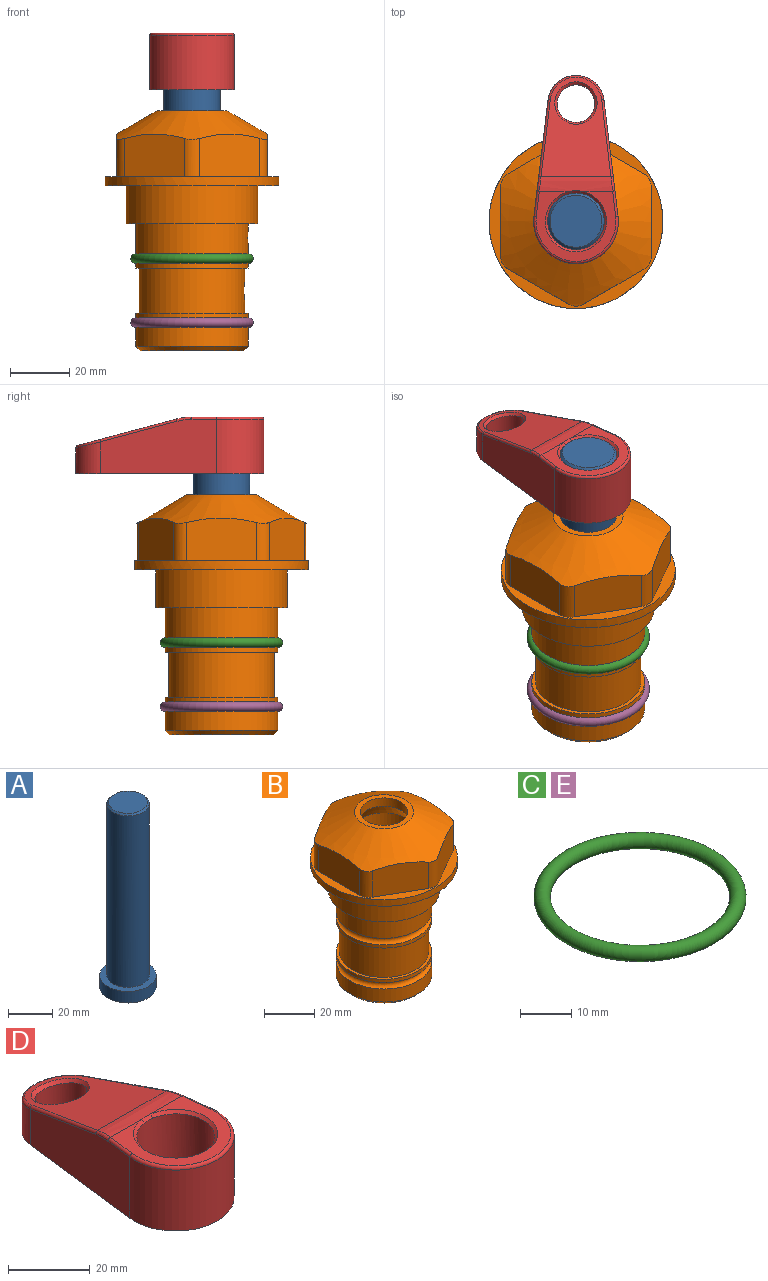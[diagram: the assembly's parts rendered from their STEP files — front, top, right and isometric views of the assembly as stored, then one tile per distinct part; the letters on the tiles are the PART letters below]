
ASSEMBLY  parts=5 mates=4
PART A: 6 faces, bbox 25.4x25.4x101.6 mm
  f0: plane 17.46x17.46mm, normal (0,0,1), area 239.5mm2, adj f5
  f1: plane 25.4x25.4mm, normal (0,0,-1), area 506.7mm2, adj f2
  f2: cylinder r=12.7mm len=25.4mm, axis (0,0,1), area 506.7mm2, adj f1,f3
  f3: plane 25.4x25.4mm, normal (0,0,1), area 221.7mm2, adj f2,f4
  f4: cylinder r=9.53mm len=94.46mm, axis (0,0,1), area 5653mm2, adj f3,f5
  f5: cone r=8.73mm half-angle=45deg, axis (0,0,-1), area 64.4mm2, adj f0,f4
PART B: 36 faces, bbox 58.7x58.7x81 mm
  f0: cylinder r=17.78mm len=35.56mm, axis (0,0,1), area 1670.8mm2, adj f23,f24,f31
  f1: cylinder r=19.05mm len=38.1mm, axis (0,0,1), area 1191.9mm2, adj f26,f27,f30
  f2: plane 58.66x58.66mm, normal (0,0,-1), area 1150.6mm2, adj f3,f28
  f3: cylinder r=29.33mm len=58.66mm, axis (0,0,-1), area 585.1mm2, adj f2,f4
  f4: plane 58.66x58.66mm, normal (0,0,1), area 475.9mm2, adj f3,f5,f6,f7,f8,f9,f10,f11
  f5: plane 20.32x14.34mm, normal (-0.5,0.87,0), area 324.4mm2, adj f4,f15,f16,f17
  f6: plane 20.32x14.34mm, normal (0.5,0.87,0), area 324.4mm2, adj f4,f14,f15,f17
  f7: plane 23.48x14.34mm, normal (1,0,0), area 324.4mm2, adj f4,f13,f14,f17
  f8: plane 20.32x14.34mm, normal (0.5,-0.87,0), area 324.4mm2, adj f4,f12,f13,f17
  f9: plane 20.32x14.34mm, normal (-0.5,-0.87,0), area 324.4mm2, adj f4,f11,f12,f17
  f10: plane 23.48x14.34mm, normal (-1,0,0), area 324.4mm2, adj f4,f11,f16,f17
  f11: cylinder r=5.08mm len=12.85mm, axis (0,0,-1), area 67.2mm2, adj f4,f9,f10,f17
  f12: cylinder r=5.08mm len=12.85mm, axis (0,0,-1), area 67.2mm2, adj f4,f8,f9,f17
  f13: cylinder r=5.08mm len=12.85mm, axis (0,0,-1), area 67.2mm2, adj f4,f7,f8,f17
  f14: cylinder r=5.08mm len=12.85mm, axis (0,0,-1), area 67.2mm2, adj f4,f6,f7,f17
  f15: cylinder r=5.08mm len=12.85mm, axis (0,0,-1), area 67.2mm2, adj f4,f5,f6,f17
  f16: cylinder r=5.08mm len=12.85mm, axis (0,0,-1), area 67.2mm2, adj f4,f5,f10,f17
  f17: cone r=11.73mm half-angle=60deg, axis (0,0,-1), area 2071.8mm2, adj f5,f6,f7,f8,f9,f10,f11,f12
  f18: plane 23.46x23.46mm, normal (0,0,1), area 147.4mm2, adj f17,f35
  f19: plane 34.93x34.93mm, normal (0,0,-1), area 958mm2, adj f29
  f20: cylinder r=19.05mm len=38.1mm, axis (0,0,1), area 760.1mm2, adj f21,f29
  f21: torus R=19.05mm, axis (0,0,1), area 565.3mm2, adj f20,f22
  f22: cylinder r=19.05mm len=38.1mm, axis (0,0,1), area 190mm2, adj f21,f23
  f23: plane 38.1x38.1mm, normal (0,0,1), area 146.9mm2, adj f0,f22
  f24: plane 38.1x38.1mm, normal (0,0,-1), area 146.9mm2, adj f0,f25
  f25: cylinder r=19.05mm len=38.1mm, axis (0,0,1), area 190mm2, adj f24,f26
  f26: torus R=19.05mm, axis (0,0,1), area 565.3mm2, adj f1,f25
  f27: plane 44.45x44.45mm, normal (0,0,-1), area 411.7mm2, adj f1,f28
  f28: cylinder r=22.23mm len=44.45mm, axis (0,0,1), area 1773.5mm2, adj f2,f27
  f29: cone r=19.05mm half-angle=45deg, axis (0,0,1), area 257.5mm2, adj f19,f20
  f30: cylinder r=3.17mm len=6.75mm, axis (-1,0,0), area 128mm2, adj f1,f33
  f31: cylinder r=3.17mm len=6.35mm, axis (-1,0,0), area 102.5mm2, adj f0,f33
  f32: plane 25.4x25.4mm, normal (0,0,1), area 506.7mm2, adj f33
  f33: cylinder r=12.7mm len=66.42mm, axis (0,0,-1), area 5236.2mm2, adj f30,f31,f32,f34
  f34: cone r=9.53mm half-angle=30deg, axis (0,0,-1), area 443.4mm2, adj f33,f35
  f35: cylinder r=9.53mm len=19.05mm, axis (0,0,-1), area 240.9mm2, adj f18,f34
PART C: 1 faces, bbox 44.7x44.7x3.2 mm
  f0: torus R=19.05mm, axis (0,0,1), area 1193.9mm2
PART D: 31 faces, bbox 31.7x65.5x19.8 mm
  f0: plane 39.12x18.26mm, normal (0.99,0.12,0), area 612.2mm2, adj f1,f4,f7,f11,f13,f15
  f1: cylinder r=9.53mm len=18.91mm, axis (0,0,-1), area 296.1mm2, adj f0,f2,f7,f17
  f2: plane 39.12x18.26mm, normal (-0.99,0.12,0), area 612.2mm2, adj f1,f4,f7,f12,f14,f16
  f3: cylinder r=6.35mm len=12.7mm, axis (0,0,-1), area 362.4mm2, adj f7,f18
  f4: cylinder r=14.29mm len=28.58mm, axis (0,0,-1), area 882.2mm2, adj f0,f2,f7,f10
  f5: cylinder r=9.53mm len=19.05mm, axis (0,0,-1), area 1092.6mm2, adj f7,f19,f20
  f6: plane 26.99x23.69mm, normal (0,0,1), area 216.2mm2, adj f9,f10,f11,f12,f19
  f7: plane 63.5x28.58mm, normal (0,0,-1), area 661.8mm2, adj f0,f1,f2,f3,f4,f5,f22,f23
  f8: plane 33.52x23.6mm, normal (0,0.26,0.97), area 486mm2, adj f9,f15,f16,f17,f18
  f9: cylinder r=19.05mm len=24.72mm, axis (1,0,0), area 120.4mm2, adj f6,f8,f13,f14,f20
  f10: torus R=13.49mm, axis (0,0,1), area 59mm2, adj f4,f6,f11,f12
  f11: cylinder r=0.79mm len=8.67mm, axis (0.12,-0.99,0), area 10.8mm2, adj f0,f6,f10,f13
  f12: cylinder r=0.79mm len=8.67mm, axis (0.12,0.99,0), area 10.8mm2, adj f2,f6,f10,f14
  f13: bspline ~4.95x1.42mm, area 6.1mm2, adj f0,f9,f11,f15
  f14: bspline ~4.95x1.42mm, area 6.1mm2, adj f2,f9,f12,f16
  f15: cylinder r=0.79mm len=25.95mm, axis (0.12,-0.96,0.26), area 32.9mm2, adj f0,f8,f13,f17
  f16: cylinder r=0.79mm len=25.95mm, axis (0.12,0.96,-0.26), area 32.9mm2, adj f2,f8,f14,f17
  f17: bspline ~18.91x8.38mm, area 30mm2, adj f1,f8,f15,f16
  f18: bspline ~14.29x14.29mm, area 48.3mm2, adj f3,f8
  f19: cone r=9.53mm half-angle=45deg, axis (0,0,1), area 66.5mm2, adj f5,f6,f20
  f20: bspline ~3.22x0.96mm, area 3.5mm2, adj f5,f9,f19
  f21: plane 2.75x2.72mm, normal (0,0,-1), area 2.9mm2, adj f23,f25,f28
  f22: plane 23.05x15.88mm, normal (-0.99,-0.12,0), area 323.6mm2, adj f7,f25,f26,f27,f28,f29
  f23: plane 23.05x15.88mm, normal (0.99,-0.12,0), area 323.6mm2, adj f7,f21,f25,f27,f28,f30
  f24: cylinder r=9.53mm len=10.69mm, axis (0,0,-1), area 114.7mm2, adj f7,f27,f29,f30
  f25: cylinder r=12.7mm len=20.59mm, axis (0,0,-1), area 381.1mm2, adj f7,f21,f22,f23,f26,f28
  f26: plane 2.75x2.72mm, normal (0,0,-1), area 2.9mm2, adj f22,f25,f28
  f27: plane 19.72x18.37mm, normal (0,-0.26,-0.97), area 291.8mm2, adj f22,f23,f24,f28,f29,f30
  f28: cylinder r=15.88mm len=19.92mm, axis (1,0,0), area 54.8mm2, adj f21,f22,f23,f25,f26,f27
  f29: cylinder r=1.59mm len=11mm, axis (0,0,-1), area 34.7mm2, adj f7,f22,f24,f27
  f30: cylinder r=1.59mm len=11mm, axis (0,0,-1), area 34.7mm2, adj f7,f23,f24,f27
PART E: same geometry as C
PLACE A t=(0,0,-11.95)mm
PLACE B at identity fixed
PLACE C at identity
PLACE D t=(0,0,-11.95)mm
PLACE E t=(0,0,-21.59)mm
MATE fastened C.f0 <-> B.f0  axis (0,0,1) through (0,0,-24.51)mm
MATE fastened A.f2 <-> D.f4  axis (0,0,1) through (0,0,51.55)mm
MATE cylindrical A.f2 <-> B.f0  axis (0,0,-1) through (0,0,-50.05)mm
MATE fastened E.f0 <-> B.f0  axis (0,0,1) through (0,0,-46.1)mm
